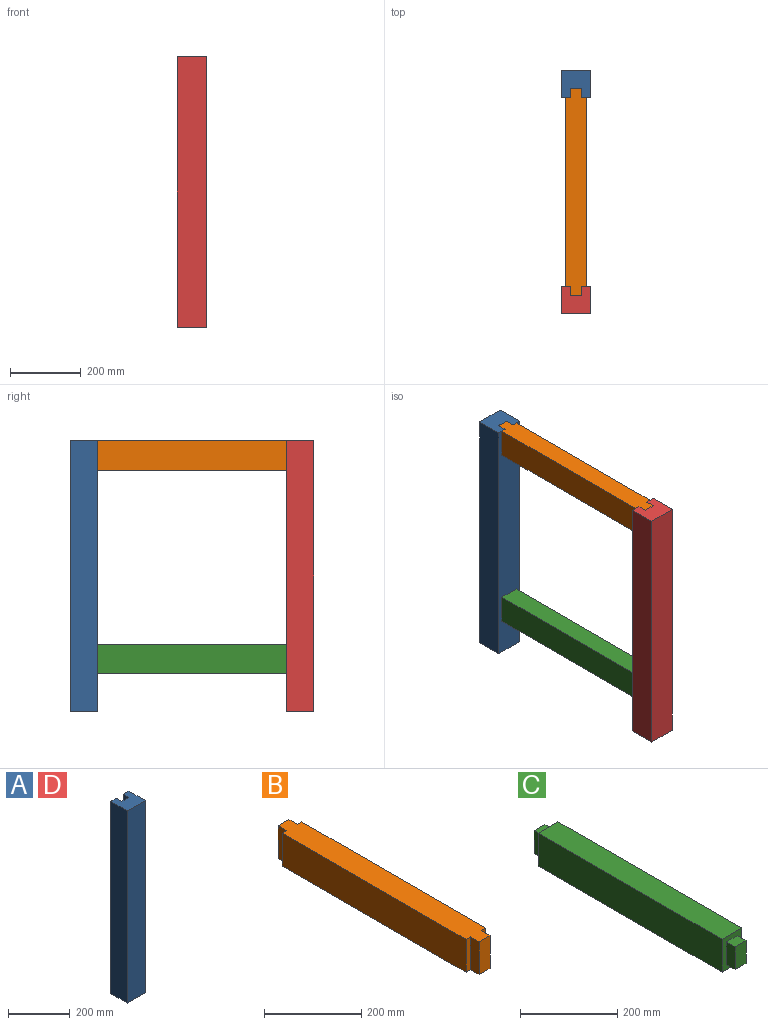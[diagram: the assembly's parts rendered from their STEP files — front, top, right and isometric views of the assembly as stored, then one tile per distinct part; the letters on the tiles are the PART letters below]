
ASSEMBLY  parts=4 mates=9
PART A: 15 faces, bbox 82.6x76.2x762 mm
  f0: plane 762x82.55mm, normal (0,1,0), area 58467.6mm2, adj f1,f2,f4,f5,f6,f7,f8,f10
  f1: plane 82.55x76.2mm, normal (0,0,1), area 5483.9mm2, adj f0,f2,f3,f4,f6,f8,f9
  f2: plane 762x76.2mm, normal (-1,0,0), area 58064.4mm2, adj f0,f1,f3,f5
  f3: plane 762x82.55mm, normal (0,-1,0), area 62903.1mm2, adj f1,f2,f4,f5
  f4: plane 762x76.2mm, normal (1,0,0), area 58064.4mm2, adj f0,f1,f3,f5
  f5: plane 82.55x76.2mm, normal (0,0,-1), area 6290.3mm2, adj f0,f2,f3,f4
  f6: plane 82.55x25.4mm, normal (-1,0,0), area 2096.8mm2, adj f0,f1,f7,f9
  f7: plane 31.75x25.4mm, normal (0,0,1), area 806.5mm2, adj f0,f6,f8,f9
  f8: plane 82.55x25.4mm, normal (1,0,0), area 2096.8mm2, adj f0,f1,f7,f9
  f9: plane 82.55x31.75mm, normal (0,1,0), area 2621mm2, adj f1,f6,f7,f8
  f10: plane 31.75x25.4mm, normal (0,0,-1), area 806.5mm2, adj f0,f11,f13,f14
  f11: plane 57.15x25.4mm, normal (-1,0,0), area 1451.6mm2, adj f0,f10,f12,f14
  f12: plane 31.75x25.4mm, normal (0,0,1), area 806.5mm2, adj f0,f11,f13,f14
  f13: plane 57.15x25.4mm, normal (1,0,0), area 1451.6mm2, adj f0,f10,f12,f14
  f14: plane 57.15x31.75mm, normal (0,1,0), area 1814.5mm2, adj f10,f11,f12,f13
PART B: 14 faces, bbox 57.2x584.2x82.6 mm
  f0: plane 584.2x57.15mm, normal (0,0,1), area 32096.8mm2, adj f2,f3,f4,f5,f6,f7,f8,f9
  f1: plane 584.2x57.15mm, normal (0,0,-1), area 32096.8mm2, adj f2,f3,f4,f5,f6,f7,f8,f9
  f2: plane 82.55x31.5mm, normal (0,1,0), area 2600mm2, adj f0,f1,f10,f12
  f3: plane 533.91x82.55mm, normal (1,0,0), area 44074.1mm2, adj f0,f1,f9,f13
  f4: plane 533.91x82.55mm, normal (-1,0,0), area 44074.1mm2, adj f0,f1,f7,f11
  f5: plane 82.55x31.5mm, normal (0,-1,0), area 2600mm2, adj f0,f1,f6,f8
  f6: plane 82.55x25.15mm, normal (-1,0,0), area 2075.8mm2, adj f0,f1,f5,f7
  f7: plane 82.55x12.95mm, normal (0,-1,0), area 1069.4mm2, adj f0,f1,f4,f6
  f8: plane 82.55x25.15mm, normal (1,0,0), area 2075.8mm2, adj f0,f1,f5,f9
  f9: plane 82.55x12.7mm, normal (0,-1,0), area 1048.4mm2, adj f0,f1,f3,f8
  f10: plane 82.55x25.15mm, normal (-1,0,0), area 2075.8mm2, adj f0,f1,f2,f11
  f11: plane 82.55x12.95mm, normal (0,1,0), area 1069.4mm2, adj f0,f1,f4,f10
  f12: plane 82.55x25.15mm, normal (1,0,0), area 2075.8mm2, adj f0,f1,f2,f13
  f13: plane 82.55x12.7mm, normal (0,1,0), area 1048.4mm2, adj f0,f1,f3,f12
PART C: 16 faces, bbox 57.2x584.2x82.6 mm
  f0: plane 533.91x57.15mm, normal (0,0,-1), area 30512.8mm2, adj f2,f3,f8,f14
  f1: plane 533.91x57.15mm, normal (0,0,1), area 30512.8mm2, adj f2,f3,f8,f14
  f2: plane 533.91x82.55mm, normal (1,0,0), area 44074.1mm2, adj f0,f1,f8,f14
  f3: plane 533.91x82.55mm, normal (-1,0,0), area 44074.1mm2, adj f0,f1,f8,f14
  f4: plane 57.15x25.15mm, normal (-1,0,0), area 1437.1mm2, adj f5,f7,f8,f9
  f5: plane 31.5x25.15mm, normal (0,0,1), area 792mm2, adj f4,f6,f8,f9
  f6: plane 57.15x25.15mm, normal (1,0,0), area 1437.1mm2, adj f5,f7,f8,f9
  f7: plane 31.5x25.15mm, normal (0,0,-1), area 792mm2, adj f4,f6,f8,f9
  f8: plane 82.55x57.15mm, normal (0,-1,0), area 2917.7mm2, adj f0,f1,f2,f3,f4,f5,f6,f7
  f9: plane 57.15x31.5mm, normal (0,-1,0), area 1800mm2, adj f4,f5,f6,f7
  f10: plane 57.15x25.15mm, normal (1,0,0), area 1437.1mm2, adj f11,f13,f14,f15
  f11: plane 31.75x25.15mm, normal (0,0,1), area 798.4mm2, adj f10,f12,f14,f15
  f12: plane 57.15x25.15mm, normal (-1,0,0), area 1437.1mm2, adj f11,f13,f14,f15
  f13: plane 31.75x25.15mm, normal (0,0,-1), area 798.4mm2, adj f10,f12,f14,f15
  f14: plane 82.55x57.15mm, normal (0,1,0), area 2903.2mm2, adj f0,f1,f2,f3,f10,f11,f12,f13
  f15: plane 57.15x31.75mm, normal (0,1,0), area 1814.5mm2, adj f10,f11,f12,f13
PART D: same geometry as A
PLACE A rot(axis=(0,0,-1),180deg) t=(112.63,2072.16,-53.45)mm
PLACE B t=(42.53,778.64,-31)mm
PLACE C t=(42.78,1016.31,-5.88)mm
PLACE D t=(30.08,1385.85,-53.45)mm
MATE planar D.f1 <-> B.f0  axis (0,0,1) through (71.36,1420.21,708.55)mm
MATE planar A.f6 <-> B.f10  axis (1,0,0) through (55.48,2008.66,667.28)mm
MATE planar B.f0 <-> A.f1  axis (0,0,1) through (42.53,1995.96,708.55)mm
MATE planar B.f9 <-> D.f0  axis (0,-1,0) through (93.33,1462.05,667.28)mm
MATE planar C.f10 <-> A.f13  axis (1,0,0) through (87.23,2021.1,93.98)mm
MATE planar B.f6 <-> D.f8  axis (-1,0,0) through (55.48,1449.48,667.28)mm
MATE planar C.f11 <-> A.f10  axis (0,0,1) through (71.36,2008.53,122.55)mm
MATE planar C.f14 <-> A.f0  axis (0,1,0) through (71.36,1995.96,93.98)mm
MATE planar B.f13 <-> A.f0  axis (0,1,0) through (93.33,1995.96,667.28)mm
